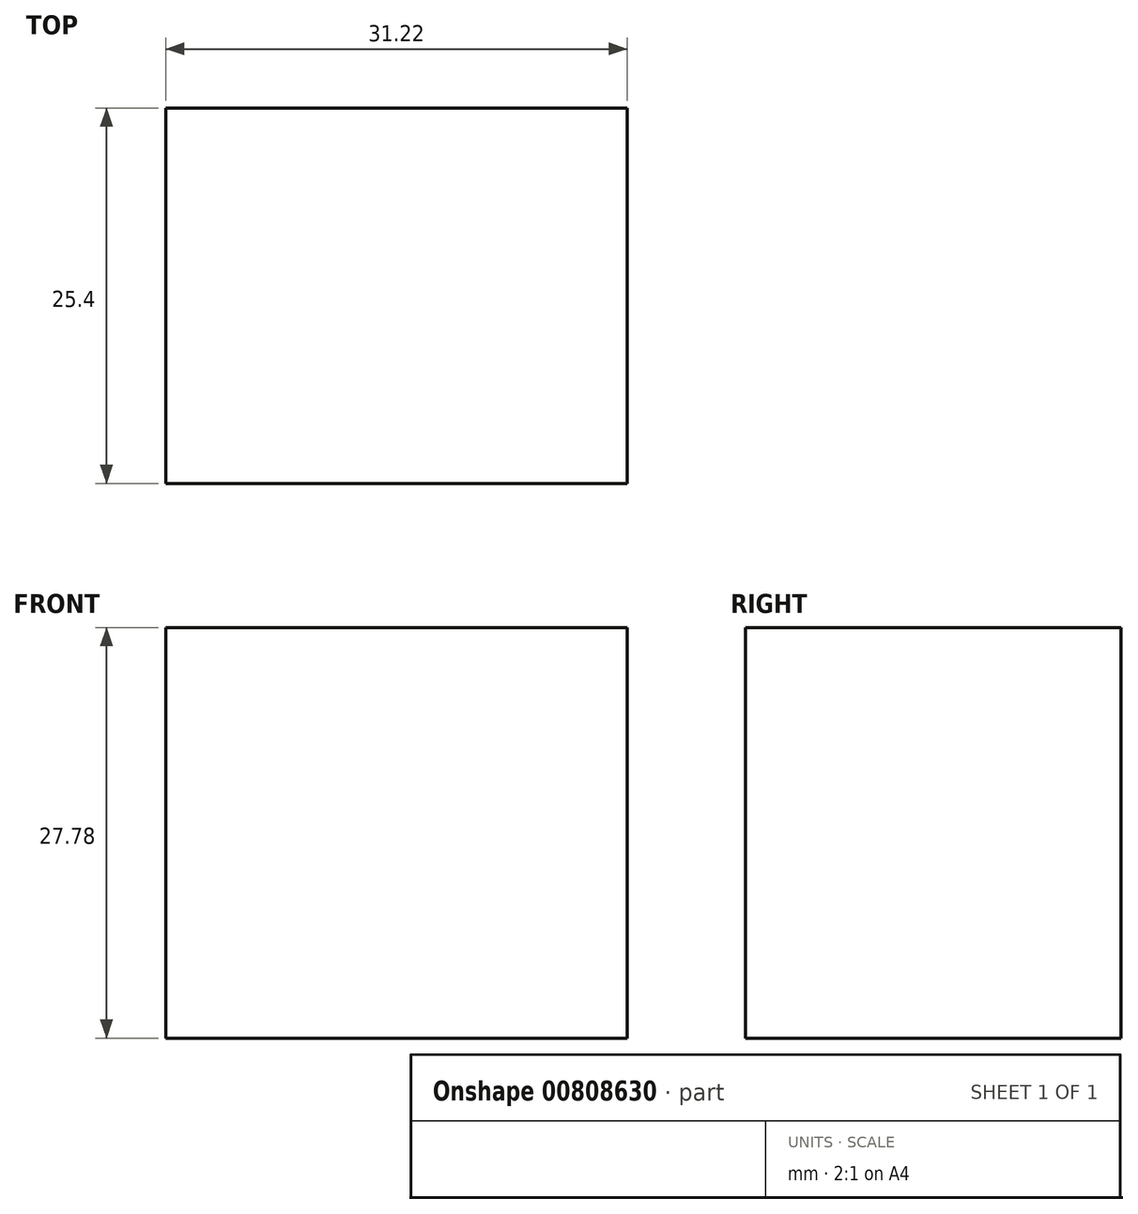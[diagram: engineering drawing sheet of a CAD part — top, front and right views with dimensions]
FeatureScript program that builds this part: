
annotation { "Feature Type Name" : "Feature", "Feature Type Description" : "" }
export const myFeature = defineFeature(function(context is Context, id is Id, definition is map)
    precondition{}
    {
        {
            var Q0;
            Q0=qCreatedBy(makeId("Front.planeOp"),FACE);
            var sketch = newSketch(context, id + "F0", { "sketchPlane" : qUnion([Q0])});
            skLineSegment(sketch, "E0.bottom", {"start": v(0, 0) * mm, "end": v(-31.22, 0) * mm});
            skLineSegment(sketch, "E0.top", {"start": v(0, 27.78) * mm, "end": v(-31.22, 27.78) * mm});
            skLineSegment(sketch, "E0.left", {"start": v(0, 0) * mm, "end": v(0, 27.78) * mm});
            skLineSegment(sketch, "E0.right", {"start": v(-31.22, 0) * mm, "end": v(-31.22, 27.78) * mm});
            skSolve(sketch);
        }
        {
            var Q0;
            Q0 = qSketchRegion(id + "F0", true);
            extrude(context, id + "F1", {"entities" : qUnion([Q0]), "depth" : 25.4 * mm, "offsetDistance" : 25.4 * mm});
        }
        {
            var Q0;
            Q0=qCreatedBy(makeId("Right.planeOp"),FACE);
            var sketch = newSketch(context, id + "F2", { "sketchPlane" : qUnion([Q0])});
            skLineSegment(sketch, "E1", {"start": v(-25.5, 27.78) * mm, "end": v(-15.56, 47.45) * mm});
            skLineSegment(sketch, "E2", {"start": v(0, 27.78) * mm, "end": v(-9.26, 47.45) * mm});
            skLineSegment(sketch, "E3", {"start": v(-15.56, 47.45) * mm, "end": v(-9.26, 47.45) * mm});
            skSolve(sketch);
        }
        {
            var Q0;
            Q0=sQuery(id+"F2.wireOp",EDGE,"E2");
            var Q1;
            Q1=sQuery(id+"F2.wireOp",EDGE,"E1");
            var Q2;
            Q2=sQuery(id+"F2.wireOp",EDGE,"E3");
            extrude(context, id + "F3", {"bodyType" : ToolBodyType.SURFACE, "surfaceEntities" : qUnion([Q0, Q1, Q2]), "depth" : 25.4 * mm, "offsetDistance" : 25.4 * mm});
        }
    });
